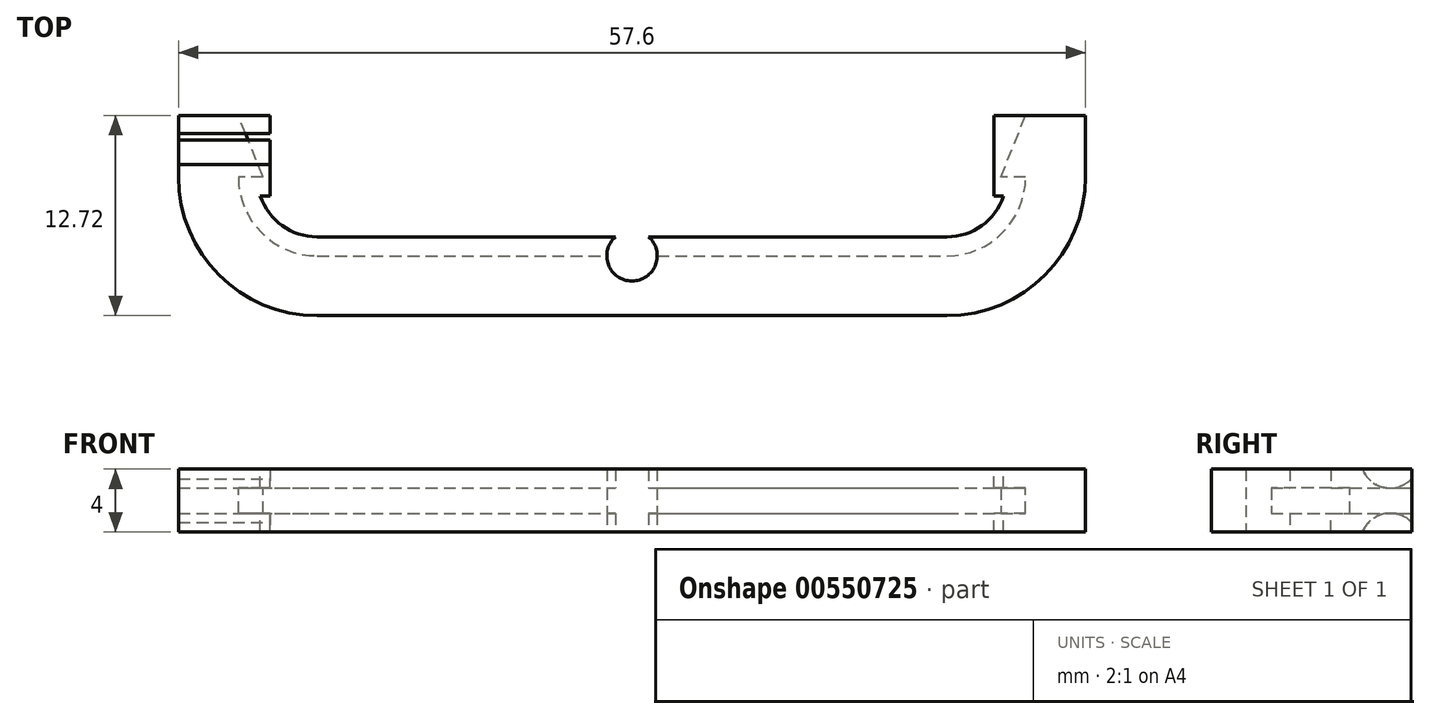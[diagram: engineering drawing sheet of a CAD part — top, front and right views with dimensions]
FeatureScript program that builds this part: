
annotation { "Feature Type Name" : "Feature", "Feature Type Description" : "" }
export const myFeature = defineFeature(function(context is Context, id is Id, definition is map)
    precondition{}
    {
        {
            var Q0;
            Q0=qCreatedBy(makeId("Right.planeOp"),FACE);
            var sketch = newSketch(context, id + "F0", { "sketchPlane" : qUnion([Q0])});
            skLineSegment(sketch, "E0", {"start": v(0, 0) * mm, "end": v(0, 2) * mm});
            skLineSegment(sketch, "E1", {"start": v(0, 2) * mm, "end": v(5, 2) * mm});
            skLineSegment(sketch, "E2", {"start": v(5, 2) * mm, "end": v(5, 0.8) * mm});
            skLineSegment(sketch, "E3", {"start": v(5, 0.8) * mm, "end": v(3.8, 0.8) * mm});
            skLineSegment(sketch, "E4", {"start": v(3.8, 0.8) * mm, "end": v(3.8, 0) * mm});
            skLineSegment(sketch, "E5.MirrorCS", {"start": v(0, 0) * mm, "end": v(0, -2) * mm});
            skLineSegment(sketch, "E6.MirrorCS", {"start": v(0, -2) * mm, "end": v(5, -2) * mm});
            skLineSegment(sketch, "E7.MirrorCS", {"start": v(3.8, -0.8) * mm, "end": v(3.8, 0) * mm});
            skLineSegment(sketch, "E8.MirrorCS", {"start": v(5, -0.8) * mm, "end": v(3.8, -0.8) * mm});
            skLineSegment(sketch, "E9.MirrorCS", {"start": v(5, -2) * mm, "end": v(5, -0.8) * mm});
            skLineSegment(sketch, "E10", {"start": v(3.8, 0.8) * mm, "end": v(3.8, 2.24) * mm, "construction": true});
            skSolve(sketch);
        }
        {
            var Q0;
            Q0=qCreatedBy(makeId("Top.planeOp"),FACE);
            var sketch = newSketch(context, id + "F1", { "sketchPlane" : qUnion([Q0])});
            skLineSegment(sketch, "E11", {"start": v(0, 0) * mm, "end": v(20, 0) * mm, "construction": true});
            skLineSegment(sketch, "E12", {"start": v(25, 8.8) * mm, "end": v(25, 13.8) * mm, "construction": true});
            skPoint(sketch, "E13.visualSharp", {"position": v(25, 0) * mm});
            skLineSegment(sketch, "E14", {"start": v(25, 8.8) * mm, "end": v(23, 8.8) * mm});
            skLineSegment(sketch, "E15", {"start": v(23, 8.8) * mm, "end": v(25, 13.8) * mm});
            skLineSegment(sketch, "E16", {"start": v(0, 3.8) * mm, "end": v(20, 3.8) * mm});
            skArc(sketch, "E17", {"start": v(20, 3.8) * mm, "mid": v(23.54, 5.26) * mm, "end": v(25, 8.8) * mm});
            skLineSegment(sketch, "E18.MirrorCS", {"start": v(0, 3.8) * mm, "end": v(-20, 3.8) * mm});
            skArc(sketch, "E19.MirrorCS", {"start": v(-20, 3.8) * mm, "mid": v(-23.54, 5.26) * mm, "end": v(-25, 8.8) * mm});
            skLineSegment(sketch, "E20.MirrorCS", {"start": v(-25, 8.8) * mm, "end": v(-23, 8.8) * mm});
            skLineSegment(sketch, "E21.MirrorCS", {"start": v(-23, 8.8) * mm, "end": v(-25, 13.8) * mm});
            skSolve(sketch);
        }
        {
            var Q0;
            Q0=makeQuery(id+"F0.imprint","IMPRINT",FACE,{"disambiguationData":[TD([[makeQuery(id+"F0.imprint","IMPRINT",EDGE,{"derivedFrom":sQuery(id+"F0.wireOp",EDGE,"E0")}),-1.0]])]});
            var Q1;
            Q1=sQuery(id+"F1.wireOp",EDGE,"E18.MirrorCS");
            var Q2;
            Q2=sQuery(id+"F1.wireOp",EDGE,"E19.MirrorCS");
            var Q3;
            Q3=sQuery(id+"F1.wireOp",EDGE,"E20.MirrorCS");
            var Q4;
            Q4=sQuery(id+"F1.wireOp",EDGE,"E16");
            var Q5;
            Q5=sQuery(id+"F1.wireOp",EDGE,"E17");
            var Q6;
            Q6=sQuery(id+"F1.wireOp",EDGE,"E14");
            sweep(context, id + "F2", {"profiles" : qUnion([Q0]), "path" : qUnion([Q1, Q2, Q3, Q4, Q5, Q6])});
        }
        {
            var Q0;
            Q0=makeQuery(id+"F2.opSweep","SWEPT_FACE",FACE,{"disambiguationData":[OSD([sQuery(id+"F0.wireOp",EDGE,"E6.MirrorCS"),sQuery(id+"F1.wireOp",EDGE,"a626e529-b565-4477-b8c0-75d9263467f50.MirrorCS")])]});
            var sketch = newSketch(context, id + "F3", { "sketchPlane" : qUnion([Q0])});
            skCircle(sketch, "E22", {"center": v(0, -3.8) * mm, "radius": 1.6 * mm});
            skCircle(sketch, "E23", {"center": v(0, -3.8) * mm, "radius": 3.2 * mm});
            skSolve(sketch);
        }
        {
            var Q0;
            {var subQ0=sQuery(id+"F3.wireOp",EDGE,"E22");var subQ1=makeQuery(id+"F2.opSweep","SWEPT_EDGE",EDGE,{"disambiguationData":[OSD([sQuery(id+"F0.wireOp",EDGE,"E6.MirrorCS"),sQuery(id+"F0.wireOp",EDGE,"E9.MirrorCS"),sQuery(id+"F1.wireOp",EDGE,"E16")])]});var subQ2=makeQuery(id+"F3.imprint","INTERSECT",VERTEX,{"disambiguationData":[OD(0.0)],"derivedFrom":[subQ1,subQ0]});Q0=makeQuery(id+"F3.imprint","IMPRINT",FACE,{"disambiguationData":[TD([[makeQuery(id+"F3.imprint","IMPRINT",EDGE,{"disambiguationData":[TD([[subQ2,1.0]])],"derivedFrom":subQ0}),1.0]])]});}
            extrude(context, id + "F4", {"entities" : qUnion([Q0]), "operationType" : NewBodyOperationType.REMOVE, "oppositeDirection" : true, "depth" : 25 * mm, "offsetDistance" : 25 * mm});
        }
        {
            assignVariable(context, id + "F5", {"name" : "Breite", "anyValue" : 0.38});
        }
        {
            var Q0;
            Q0=makeQuery(id+"F2.opSweep","SWEPT_FACE",FACE,{"disambiguationData":[OSD([sQuery(id+"F0.wireOp",EDGE,"E0"),sQuery(id+"F0.wireOp",EDGE,"E5.MirrorCS"),sQuery(id+"F1.wireOp",EDGE,"E20.MirrorCS")])]});
            var Q1;
            Q1=makeQuery(id+"F2.opSweep","SWEPT_FACE",FACE,{"disambiguationData":[OSD([sQuery(id+"F0.wireOp",EDGE,"E0"),sQuery(id+"F0.wireOp",EDGE,"E5.MirrorCS"),sQuery(id+"F1.wireOp",EDGE,"E14")])]});
            extrude(context, id + "F6", {"entities" : qUnion([Q0, Q1]), "operationType" : NewBodyOperationType.ADD, "depth" : (0.5 - getVariable(context, 'Breite')) * mm, "offsetDistance" : 25 * mm});
        }
        {
            var Q0;
            Q0=makeQuery(id+"F6.opExtrude","CAP_FACE",FACE,{"disambiguationData":[OSD([sQuery(id+"F0.wireOp",EDGE,"E0"),sQuery(id+"F0.wireOp",EDGE,"E1"),sQuery(id+"F0.wireOp",EDGE,"E5.MirrorCS"),sQuery(id+"F0.wireOp",EDGE,"E6.MirrorCS"),sQuery(id+"F1.wireOp",VERTEX,"E14.start"),sQuery(id+"F1.wireOp",VERTEX,"E14.end"),sQuery(id+"F1.wireOp",EDGE,"E14")])],"isStart":false});
            var sketch = newSketch(context, id + "F7", { "sketchPlane" : qUnion([Q0])});
            skLineSegment(sketch, "E24", {"start": v(-23, 0.8) * mm, "end": v(-25, 0.8) * mm});
            skLineSegment(sketch, "E25", {"start": v(-25, 0.8) * mm, "end": v(-25, -0.8) * mm});
            skLineSegment(sketch, "E26", {"start": v(-25, -0.8) * mm, "end": v(-23, -0.8) * mm});
            skLineSegment(sketch, "E27.MirrorCS", {"start": v(25, -0.8) * mm, "end": v(23, -0.8) * mm});
            skLineSegment(sketch, "E28.MirrorCS", {"start": v(25, 0.8) * mm, "end": v(25, -0.8) * mm});
            skLineSegment(sketch, "E29.MirrorCS", {"start": v(23, 0.8) * mm, "end": v(25, 0.8) * mm});
            skSolve(sketch);
        }
        {
            var Q0;
            {var subQ0=sQuery(id+"F7.wireOp",EDGE,"E24");Q0=makeQuery(id+"F7.imprint","IMPRINT",FACE,{"disambiguationData":[TD([[makeQuery(id+"F7.imprint","IMPRINT",EDGE,{"derivedFrom":subQ0}),1.0]])]});}
            var Q1;
            Q1=sQuery(id+"F1.wireOp",EDGE,"E15");
            sweep(context, id + "F8", {"operationType" : NewBodyOperationType.REMOVE, "profiles" : qUnion([Q0]), "path" : qUnion([Q1])});
        }
        {
            var Q0;
            Q0=makeQuery(id+"F6.opExtrude","CAP_FACE",FACE,{"disambiguationData":[OSD([sQuery(id+"F0.wireOp",EDGE,"E0"),sQuery(id+"F0.wireOp",EDGE,"E5.MirrorCS"),sQuery(id+"F1.wireOp",EDGE,"E20.MirrorCS")])],"isStart":false});
            var sketch = newSketch(context, id + "F9", { "sketchPlane" : qUnion([Q0])});
            skLineSegment(sketch, "E30", {"start": v(23, -0.8) * mm, "end": v(25, -0.8) * mm});
            skLineSegment(sketch, "E31", {"start": v(25, -0.8) * mm, "end": v(25, 0.8) * mm});
            skLineSegment(sketch, "E32", {"start": v(25, 0.8) * mm, "end": v(23, 0.8) * mm});
            skSolve(sketch);
        }
        {
            var Q0;
            Q0=qSketchRegion(id+"F7",true);
            var Q1;
            {var subQ0=sQuery(id+"F9.wireOp",EDGE,"E30");Q1=makeQuery(id+"F9.imprint","IMPRINT",FACE,{"disambiguationData":[TD([[makeQuery(id+"F9.imprint","IMPRINT",EDGE,{"derivedFrom":subQ0}),1.0]])]});}
            var Q2;
            Q2=sQuery(id+"F1.wireOp",EDGE,"E21.MirrorCS");
            sweep(context, id + "F10", {"operationType" : NewBodyOperationType.REMOVE, "profiles" : qUnion([Q0, Q1]), "path" : qUnion([Q2])});
        }
        {
            var Q0;
            {var subQ0=sQuery(id+"F1.wireOp",EDGE,"E20.MirrorCS");var subQ1=sQuery(id+"F0.wireOp",EDGE,"E7.MirrorCS");var subQ2=sQuery(id+"F0.wireOp",EDGE,"E4");var subQ3=sQuery(id+"F0.wireOp",EDGE,"E1");var subQ4=sQuery(id+"F0.wireOp",EDGE,"E3");var subQ5=sQuery(id+"F0.wireOp",EDGE,"E2");var subQ7=sQuery(id+"F0.wireOp",EDGE,"E0");var subQ8=sQuery(id+"F0.wireOp",EDGE,"E5.MirrorCS");var subQ9=sQuery(id+"F1.wireOp",VERTEX,"E20.MirrorCS.end");Q0=makeQuery(id+"F10.boolean.opBoolean","SPLIT",FACE,{"disambiguationData":[TD([makeQuery(id+"F2.opSweep","SWEPT_FACE",FACE,{"disambiguationData":[OSD([subQ3,subQ0])]})])],"derivedFrom":makeQuery(id+"F6.boolean.opBoolean","MERGE",FACE,{"derivedFrom":[makeQuery(id+"F2.opSweep","CAP_FACE",FACE,{"disambiguationData":[OSD([subQ7,subQ3,subQ5,subQ4,subQ2,subQ8,sQuery(id+"F0.wireOp",EDGE,"E6.MirrorCS"),subQ1,sQuery(id+"F0.wireOp",EDGE,"E8.MirrorCS"),sQuery(id+"F0.wireOp",EDGE,"E9.MirrorCS"),subQ9])],"isStart":true}),makeQuery(id+"F6.opExtrude","SWEPT_FACE",FACE,{"disambiguationData":[OSD([subQ7,subQ8,subQ9])]})]})});}
            var sketch = newSketch(context, id + "F11", { "sketchPlane" : qUnion([Q0])});
            skLineSegment(sketch, "E33", {"start": v(7.6, 2) * mm, "end": v(9.6, 2) * mm});
            skLineSegment(sketch, "E34", {"start": v(13.8, 2) * mm, "end": v(13.1, 2) * mm});
            skArc(sketch, "E35", {"start": v(9.6, 2) * mm, "mid": v(11.35, 0.79) * mm, "end": v(13.1, 2) * mm});
            skSolve(sketch);
        }
        {
            var Q0;
            {var subQ0=sQuery(id+"F11.wireOp",EDGE,"E35");var subQ1=sQuery(id+"F0.wireOp",EDGE,"E1");var subQ2=sQuery(id+"F0.wireOp",EDGE,"E0");var subQ3=sQuery(id+"F1.wireOp",VERTEX,"E20.MirrorCS.end");var subQ4=makeQuery(id+"F6.boolean.opBoolean","MERGE",EDGE,{"derivedFrom":[makeQuery(id+"F2.opSweep","CAP_EDGE",EDGE,{"disambiguationData":[OSD([subQ1,subQ3])],"isStart":true}),makeQuery(id+"F6.opExtrude","SWEPT_EDGE",EDGE,{"disambiguationData":[OSD([subQ2,subQ1,sQuery(id+"F1.wireOp",EDGE,"E20.MirrorCS")])]})]});var subQ5=makeQuery(id+"F11.imprint","INTERSECT",VERTEX,{"derivedFrom":[subQ4,sQuery(id+"F11.wireOp",EDGE,"E33"),subQ0]});Q0=makeQuery(id+"F11.imprint","IMPRINT",FACE,{"disambiguationData":[TD([[makeQuery(id+"F11.imprint","IMPRINT",EDGE,{"disambiguationData":[TD([[subQ5,-1.0]])],"derivedFrom":subQ4}),-1.0]])]});}
            extrude(context, id + "F12", {"entities" : qUnion([Q0]), "operationType" : NewBodyOperationType.REMOVE, "oppositeDirection" : true, "depth" : 25 * mm, "offsetDistance" : 25 * mm});
        }
        {
            var Q0;
            {var subQ0=sQuery(id+"F1.wireOp",EDGE,"E20.MirrorCS");var subQ1=sQuery(id+"F0.wireOp",EDGE,"E9.MirrorCS");var subQ2=sQuery(id+"F0.wireOp",EDGE,"E8.MirrorCS");var subQ3=sQuery(id+"F0.wireOp",EDGE,"E5.MirrorCS");var subQ4=sQuery(id+"F0.wireOp",EDGE,"E0");var subQ5=sQuery(id+"F0.wireOp",EDGE,"E6.MirrorCS");var subQ6=sQuery(id+"F0.wireOp",EDGE,"E7.MirrorCS");var subQ7=sQuery(id+"F0.wireOp",EDGE,"E4");var subQ9=sQuery(id+"F1.wireOp",VERTEX,"E20.MirrorCS.end");Q0=makeQuery(id+"F10.boolean.opBoolean","SPLIT",FACE,{"disambiguationData":[TD([makeQuery(id+"F2.opSweep","SWEPT_FACE",FACE,{"disambiguationData":[OSD([subQ5,subQ0])]})])],"derivedFrom":makeQuery(id+"F6.boolean.opBoolean","MERGE",FACE,{"derivedFrom":[makeQuery(id+"F2.opSweep","CAP_FACE",FACE,{"disambiguationData":[OSD([subQ4,sQuery(id+"F0.wireOp",EDGE,"E1"),sQuery(id+"F0.wireOp",EDGE,"E2"),sQuery(id+"F0.wireOp",EDGE,"E3"),subQ7,subQ3,subQ5,subQ6,subQ2,subQ1,subQ9])],"isStart":true}),makeQuery(id+"F6.opExtrude","SWEPT_FACE",FACE,{"disambiguationData":[OSD([subQ4,subQ3,subQ9])]})]})});}
            var sketch = newSketch(context, id + "F13", { "sketchPlane" : qUnion([Q0])});
            skLineSegment(sketch, "E36", {"start": v(7.6, -2) * mm, "end": v(9.6, -2) * mm});
            skLineSegment(sketch, "E37", {"start": v(13.1, -2) * mm, "end": v(13.8, -2) * mm});
            skArc(sketch, "E38", {"start": v(13.1, -2) * mm, "mid": v(11.35, -0.79) * mm, "end": v(9.6, -2) * mm});
            skSolve(sketch);
        }
        {
            var Q0;
            {var subQ0=sQuery(id+"F13.wireOp",EDGE,"E38");var subQ1=sQuery(id+"F0.wireOp",EDGE,"E6.MirrorCS");var subQ2=sQuery(id+"F0.wireOp",EDGE,"E5.MirrorCS");var subQ3=sQuery(id+"F1.wireOp",VERTEX,"E20.MirrorCS.end");var subQ4=makeQuery(id+"F6.boolean.opBoolean","MERGE",EDGE,{"derivedFrom":[makeQuery(id+"F2.opSweep","CAP_EDGE",EDGE,{"disambiguationData":[OSD([subQ1,subQ3])],"isStart":true}),makeQuery(id+"F6.opExtrude","SWEPT_EDGE",EDGE,{"disambiguationData":[OSD([subQ2,subQ1,sQuery(id+"F1.wireOp",EDGE,"E20.MirrorCS")])]})]});var subQ9=makeQuery(id+"F13.imprint","INTERSECT",VERTEX,{"derivedFrom":[subQ4,sQuery(id+"F13.wireOp",EDGE,"E36"),subQ0]});Q0=makeQuery(id+"F13.imprint","IMPRINT",FACE,{"disambiguationData":[TD([[makeQuery(id+"F13.imprint","IMPRINT",EDGE,{"disambiguationData":[TD([[subQ9,1.0]])],"derivedFrom":subQ4}),-1.0]])]});}
            extrude(context, id + "F14", {"entities" : qUnion([Q0]), "operationType" : NewBodyOperationType.REMOVE, "oppositeDirection" : true, "depth" : 25 * mm, "offsetDistance" : 25 * mm});
        }
    });
